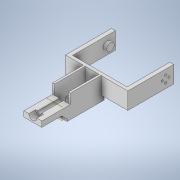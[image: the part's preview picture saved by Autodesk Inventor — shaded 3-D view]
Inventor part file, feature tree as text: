
AUTODESK INVENTOR PART (.ipt)
format: ipt  version: 2022 (Build 260153000, 153)  size: 237,056 bytes
history: native  units: mm
features: extrude x12, sketch x12, plane x1
ambient origin geometry x8: Origin, YZ Plane, XZ Plane, XY Plane, X Axis, Y Axis, Z Axis, Center Point
bodies: Solid1 (feature_tree)
feature tree (25):
  extrude  "Extrusion1"  Depth=25.4mm TaperAngle=0.0deg
  extrude  "Extrusion2"  Depth=3.0mm
  extrude  "Extrusion3"  Depth=46.0mm
  extrude  "Extrusion4"  Depth=34.33mm
  extrude  "Extrusion5"  Depth=7.0mm
  extrude  "Extrusion6"  Depth=6.0mm
  extrude  "Extrusion7"  Depth=5.0mm
  extrude  "Extrusion8"  Depth=16.63mm
  extrude  "Extrusion9"  Depth=6.0mm
  extrude  "Extrusion10"  Depth=12.0mm
  extrude  "Extrusion13"  Depth=7.0mm
  extrude  "Extrusion14"  Depth=7.0mm TaperAngle=0.0deg
  plane  "Work Plane6"
  sketch  "Sketch1"  dims[d4=69.0mm d5=25.4mm d6=0.0mm]
  sketch  "Sketch2"  dims[d19=3.0mm d20=10.35mm]
  sketch  "Sketch3"  dims[d22=46.0mm d23=0.0mm d24=10.35mm]
  sketch  "Sketch4"  dims[d25=10.35mm d26=34.33mm]
  sketch  "Sketch5"  dims[d27=31.33mm d28=0.0mm d30=7.0mm]
  sketch  "Sketch6"  dims[d31=6.0mm d32=0.0mm d35=2.0mm]
  sketch  "Sketch7"  dims[d36=0.0mm d37=0.0mm d41=5.0mm]
  sketch  "Sketch8"  dims[d42=16.63mm d46=30.0mm]
  sketch  "Sketch9"  dims[d47=10.0mm d48=0.0mm d49=6.0mm]
  sketch  "Sketch10"  dims[d50=0.0mm d51=0.0mm d52=12.0mm]
  sketch  "Sketch13"  dims[d53=10.0mm d54=0.0mm d55=7.0mm]
  sketch  "Sketch14"  dims[d56=7.0mm d57=7.0mm d58=5.0mm d59=0.0mm d60=0.0mm d61=7.0mm d62=0.0mm d76=11.5mm d77=5.0mm d78=0.0mm d80=3.0mm d81=40.0mm d83=360.0deg d85=5.0mm d86=0.0mm d87=-10.0mm]
